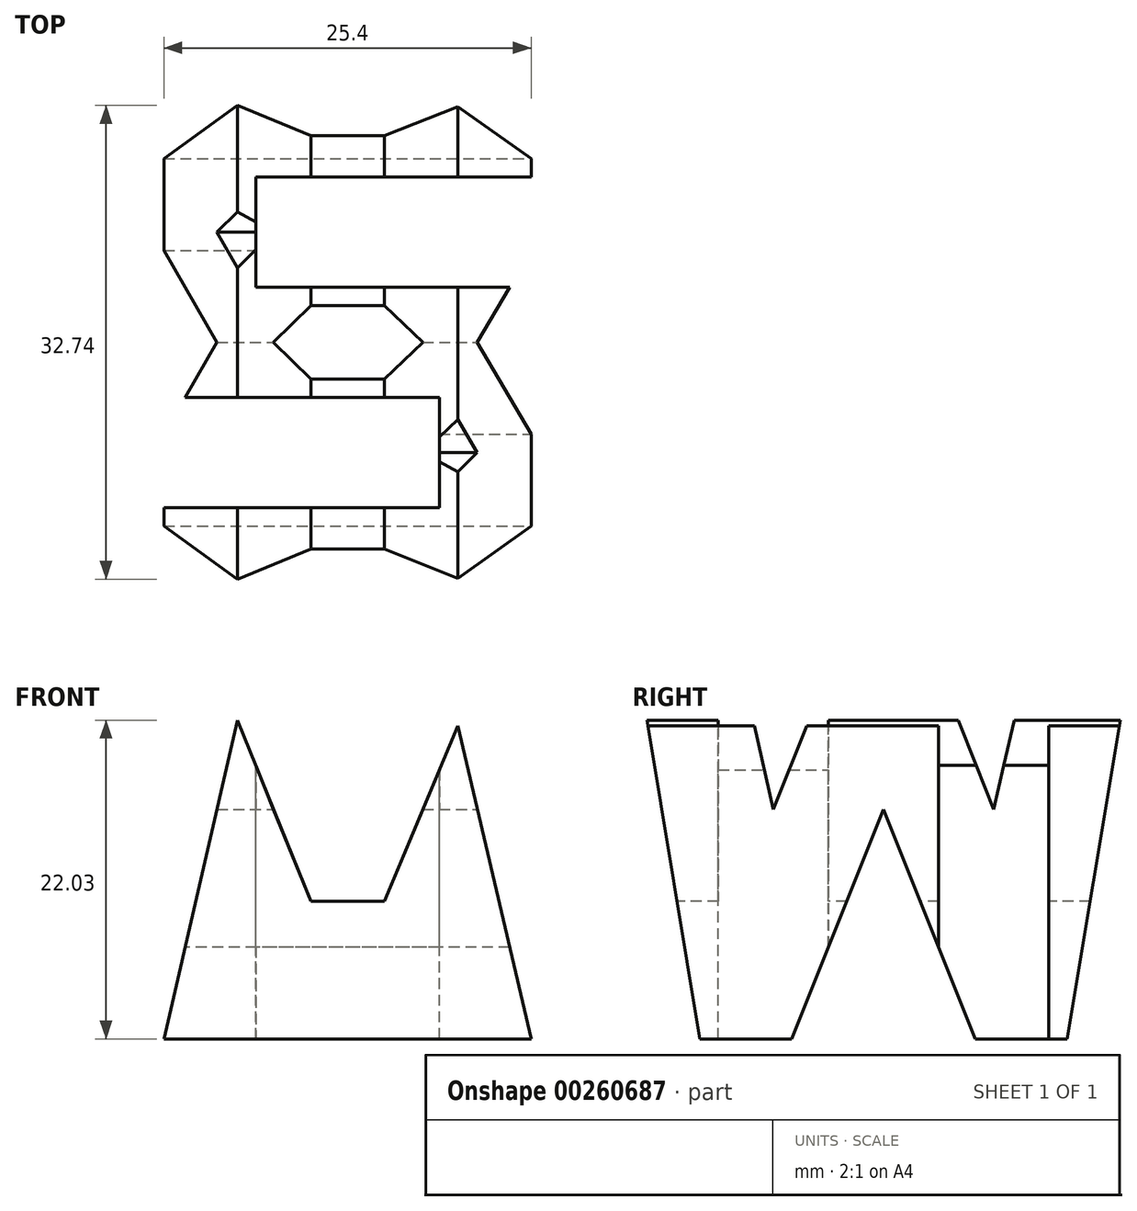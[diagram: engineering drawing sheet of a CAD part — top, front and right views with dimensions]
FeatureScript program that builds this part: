
annotation { "Feature Type Name" : "Feature", "Feature Type Description" : "" }
export const myFeature = defineFeature(function(context is Context, id is Id, definition is map)
    precondition{}
    {
        {
            var Q0;
            Q0=qCreatedBy(makeId("Front.planeOp"),FACE);
            var sketch = newSketch(context, id + "F0", { "sketchPlane" : qUnion([Q0])});
            skLineSegment(sketch, "E0", {"start": v(0, 0) * mm, "end": v(38.1, 0) * mm});
            skLineSegment(sketch, "E1", {"start": v(38.1, 0) * mm, "end": v(38.1, 38.1) * mm});
            skLineSegment(sketch, "E2", {"start": v(38.1, 38.1) * mm, "end": v(0, 38.1) * mm});
            skLineSegment(sketch, "E3", {"start": v(0, 38.1) * mm, "end": v(0, 0) * mm});
            skSolve(sketch);
        }
        {
            var Q0;
            Q0=makeQuery(id+"F0.imprint","IMPRINT",FACE,{"disambiguationData":[TD([[makeQuery(id+"F0.imprint","IMPRINT",EDGE,{"derivedFrom":sQuery(id+"F0.wireOp",EDGE,"E0")}),1.0]])]});
            extrude(context, id + "F1", {"entities" : qUnion([Q0]), "depth" : 38.1 * mm});
        }
        {
            var Q0;
            Q0=qCreatedBy(makeId("Front.planeOp"),FACE);
            cPlane(context, id + "F2", {"entities" : qUnion([Q0]), "cplaneType" : CPlaneType.OFFSET, "offset" : 38.1 * mm, "width" : 152.4 * mm, "height" : 152.4 * mm});
        }
        {
            var Q0;
            Q0=qCreatedBy(makeId("Right.planeOp"),FACE);
            cPlane(context, id + "F3", {"entities" : qUnion([Q0]), "cplaneType" : CPlaneType.OFFSET, "offset" : 38.1 * mm, "width" : 152.4 * mm, "height" : 152.4 * mm});
        }
        {
            var Q0;
            Q0=qCreatedBy(makeId("Top.planeOp"),FACE);
            cPlane(context, id + "F4", {"entities" : qUnion([Q0]), "cplaneType" : CPlaneType.OFFSET, "offset" : 38.1 * mm, "width" : 152.4 * mm, "height" : 152.4 * mm});
        }
        {
            var Q0;
            Q0=qCreatedBy(id+"F3.planeOp",FACE);
            var sketch = newSketch(context, id + "F5", { "sketchPlane" : qUnion([Q0])});
            skLineSegment(sketch, "E4", {"start": v(0, 0) * mm, "end": v(-38.1, 0) * mm});
            skLineSegment(sketch, "E5", {"start": v(-38.1, 0) * mm, "end": v(-38.1, 38.1) * mm});
            skLineSegment(sketch, "E6", {"start": v(-38.1, 38.1) * mm, "end": v(0, 38.1) * mm});
            skLineSegment(sketch, "E7", {"start": v(0, 38.1) * mm, "end": v(0, 0) * mm});
            skLineSegment(sketch, "E8", {"start": v(-31.75, 0) * mm, "end": v(-25.4, 0) * mm});
            skLineSegment(sketch, "E9", {"start": v(-12.7, 0) * mm, "end": v(-6.35, 0) * mm});
            skLineSegment(sketch, "E10", {"start": v(-38.1, 38.1) * mm, "end": v(-31.75, 0) * mm});
            skLineSegment(sketch, "E11", {"start": v(-25.4, 0) * mm, "end": v(-19.05, 15.88) * mm});
            skLineSegment(sketch, "E12", {"start": v(-19.05, 15.88) * mm, "end": v(-12.7, 0) * mm});
            skLineSegment(sketch, "E13", {"start": v(-6.35, 0) * mm, "end": v(-12.7, 0) * mm});
            skLineSegment(sketch, "E14", {"start": v(-6.35, 0) * mm, "end": v(0, 38.1) * mm});
            skLineSegment(sketch, "E15", {"start": v(-6.35, 38.1) * mm, "end": v(-11.43, 15.87) * mm});
            skLineSegment(sketch, "E16", {"start": v(-11.43, 15.88) * mm, "end": v(-16.5, 28.57) * mm});
            skLineSegment(sketch, "E17", {"start": v(-16.5, 28.57) * mm, "end": v(-21.59, 28.57) * mm});
            skLineSegment(sketch, "E18", {"start": v(-21.59, 28.57) * mm, "end": v(-26.67, 15.87) * mm});
            skLineSegment(sketch, "E19", {"start": v(-26.67, 15.87) * mm, "end": v(-31.75, 38.1) * mm});
            skLineSegment(sketch, "E20", {"start": v(-31.75, 38.1) * mm, "end": v(-38.1, 38.1) * mm});
            skSolve(sketch);
        }
        {
            var Q0;
            {var subQ0=sQuery(id+"F5.wireOp",EDGE,"E15");Q0=makeQuery(id+"F5.imprint","IMPRINT",FACE,{"disambiguationData":[TD([[makeQuery(id+"F5.imprint","IMPRINT",EDGE,{"derivedFrom":subQ0}),-1.0]])]});}
            var Q1;
            {var subQ0=sQuery(id+"F5.wireOp",EDGE,"E5");Q1=makeQuery(id+"F5.imprint","IMPRINT",FACE,{"disambiguationData":[TD([[makeQuery(id+"F5.imprint","IMPRINT",EDGE,{"derivedFrom":subQ0}),-1.0]])]});}
            var Q2;
            {var subQ0=sQuery(id+"F5.wireOp",EDGE,"E11");Q2=makeQuery(id+"F5.imprint","IMPRINT",FACE,{"disambiguationData":[TD([[makeQuery(id+"F5.imprint","IMPRINT",EDGE,{"derivedFrom":subQ0}),-1.0]])]});}
            var Q3;
            {var subQ0=sQuery(id+"F5.wireOp",EDGE,"E7");Q3=makeQuery(id+"F5.imprint","IMPRINT",FACE,{"disambiguationData":[TD([[makeQuery(id+"F5.imprint","IMPRINT",EDGE,{"derivedFrom":subQ0}),-1.0]])]});}
            extrude(context, id + "F6", {"entities" : qUnion([Q0, Q1, Q2, Q3]), "operationType" : NewBodyOperationType.REMOVE, "oppositeDirection" : true, "depth" : 38.1 * mm});
        }
        {
            var Q0;
            Q0=qCreatedBy(id+"F2.planeOp",FACE);
            var sketch = newSketch(context, id + "F7", { "sketchPlane" : qUnion([Q0])});
            skLineSegment(sketch, "E21", {"start": v(0, 0) * mm, "end": v(0, 38.1) * mm});
            skLineSegment(sketch, "E22", {"start": v(0, 38.1) * mm, "end": v(38.1, 38.1) * mm});
            skLineSegment(sketch, "E23", {"start": v(38.1, 38.1) * mm, "end": v(38.1, 0) * mm});
            skLineSegment(sketch, "E24", {"start": v(38.1, 0) * mm, "end": v(0, 0) * mm});
            skLineSegment(sketch, "E25", {"start": v(0, 0) * mm, "end": v(6.35, 38.1) * mm});
            skLineSegment(sketch, "E26", {"start": v(6.35, 38.1) * mm, "end": v(12.7, 38.1) * mm});
            skLineSegment(sketch, "E27", {"start": v(12.7, 38.1) * mm, "end": v(19.05, 22.23) * mm});
            skLineSegment(sketch, "E28", {"start": v(19.05, 22.23) * mm, "end": v(25.4, 38.1) * mm});
            skLineSegment(sketch, "E29", {"start": v(25.4, 38.1) * mm, "end": v(31.75, 38.1) * mm});
            skLineSegment(sketch, "E30", {"start": v(31.75, 38.1) * mm, "end": v(38.1, 0) * mm});
            skLineSegment(sketch, "E31", {"start": v(38.1, 0) * mm, "end": v(31.75, 0) * mm});
            skLineSegment(sketch, "E32", {"start": v(21.59, 9.53) * mm, "end": v(16.51, 9.53) * mm});
            skLineSegment(sketch, "E33", {"start": v(6.35, 0) * mm, "end": v(0, 0) * mm});
            skLineSegment(sketch, "E34", {"start": v(6.35, 0) * mm, "end": v(11.43, 22.03) * mm});
            skLineSegment(sketch, "E35", {"start": v(11.43, 22.03) * mm, "end": v(16.51, 9.53) * mm});
            skLineSegment(sketch, "E36", {"start": v(31.75, 0) * mm, "end": v(26.67, 21.63) * mm});
            skLineSegment(sketch, "E37", {"start": v(21.59, 9.53) * mm, "end": v(26.67, 21.63) * mm});
            skSolve(sketch);
        }
        {
            var Q0;
            {var subQ0=sQuery(id+"F7.wireOp",EDGE,"E21");Q0=makeQuery(id+"F7.imprint","IMPRINT",FACE,{"disambiguationData":[TD([[makeQuery(id+"F7.imprint","IMPRINT",EDGE,{"derivedFrom":subQ0}),-1.0]])]});}
            var Q1;
            {var subQ0=sQuery(id+"F7.wireOp",EDGE,"E27");Q1=makeQuery(id+"F7.imprint","IMPRINT",FACE,{"disambiguationData":[TD([[makeQuery(id+"F7.imprint","IMPRINT",EDGE,{"derivedFrom":subQ0}),1.0]])]});}
            var Q2;
            {var subQ0=sQuery(id+"F7.wireOp",EDGE,"E23");Q2=makeQuery(id+"F7.imprint","IMPRINT",FACE,{"disambiguationData":[TD([[makeQuery(id+"F7.imprint","IMPRINT",EDGE,{"derivedFrom":subQ0}),-1.0]])]});}
            var Q3;
            Q3=makeQuery(id+"F7.imprint","IMPRINT",FACE,{"disambiguationData":[TD([[makeQuery(id+"F7.imprint","IMPRINT",EDGE,{"derivedFrom":sQuery(id+"F7.wireOp",EDGE,"E24")}),-1.0]])]});
            extrude(context, id + "F8", {"entities" : qUnion([Q0, Q1, Q2, Q3]), "operationType" : NewBodyOperationType.REMOVE, "oppositeDirection" : true, "depth" : 38.1 * mm});
        }
        {
            var Q0;
            Q0=qCreatedBy(id+"F4.planeOp",FACE);
            var sketch = newSketch(context, id + "F9", { "sketchPlane" : qUnion([Q0])});
            skLineSegment(sketch, "E38", {"start": v(0, 0) * mm, "end": v(38.1, 0) * mm});
            skLineSegment(sketch, "E39", {"start": v(38.1, 0) * mm, "end": v(38.1, -38.1) * mm});
            skLineSegment(sketch, "E40", {"start": v(38.1, -38.1) * mm, "end": v(0, -38.1) * mm});
            skLineSegment(sketch, "E41", {"start": v(0, -38.1) * mm, "end": v(0, 0) * mm});
            skLineSegment(sketch, "E42", {"start": v(38.1, -7.62) * mm, "end": v(12.7, -7.62) * mm});
            skLineSegment(sketch, "E43", {"start": v(12.7, -7.62) * mm, "end": v(12.7, -15.24) * mm});
            skLineSegment(sketch, "E44", {"start": v(12.7, -15.24) * mm, "end": v(38.1, -15.24) * mm});
            skLineSegment(sketch, "E45", {"start": v(0, -22.86) * mm, "end": v(25.4, -22.86) * mm});
            skLineSegment(sketch, "E46", {"start": v(25.4, -22.86) * mm, "end": v(25.4, -30.48) * mm});
            skLineSegment(sketch, "E47", {"start": v(25.4, -30.48) * mm, "end": v(0, -30.48) * mm});
            skSolve(sketch);
        }
        {
            var Q0;
            {var subQ0=sQuery(id+"F9.wireOp",EDGE,"E42");Q0=makeQuery(id+"F9.imprint","IMPRINT",FACE,{"disambiguationData":[TD([[makeQuery(id+"F9.imprint","IMPRINT",EDGE,{"derivedFrom":subQ0}),1.0]])]});}
            var Q1;
            {var subQ0=sQuery(id+"F9.wireOp",EDGE,"E45");Q1=makeQuery(id+"F9.imprint","IMPRINT",FACE,{"disambiguationData":[TD([[makeQuery(id+"F9.imprint","IMPRINT",EDGE,{"derivedFrom":subQ0}),-1.0]])]});}
            extrude(context, id + "F10", {"entities" : qUnion([Q0, Q1]), "operationType" : NewBodyOperationType.REMOVE, "oppositeDirection" : true, "depth" : 38.1 * mm});
        }
    });
